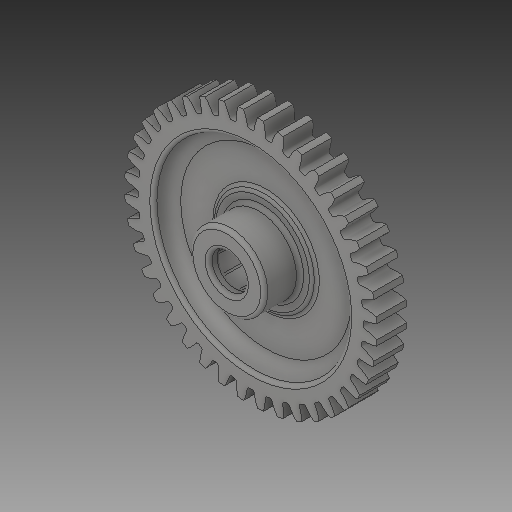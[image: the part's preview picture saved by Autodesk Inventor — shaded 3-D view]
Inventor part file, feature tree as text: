
AUTODESK INVENTOR PART (.ipt)
format: ipt  version: 2017 (Build 210142000, 142)  size: 623,104 bytes
history: native  units: in
note: dims shown in document units (in); Inventor stores cm internally (conversion verified against a paired STEP export)
features: fillet x1
ambient origin geometry x8: Origin, YZ Plane, XZ Plane, XY Plane, X Axis, Y Axis, Z Axis, Center Point
bodies: Solid1 (feature_tree)
feature tree (1):
  fillet  "Fillet4"  [1 undecoded]
note: 1 required parameter value undecoded (feature->parameter linkage not recoverable at this tier; creation-order binding heuristic only, values carry confidence <= 0.55)
